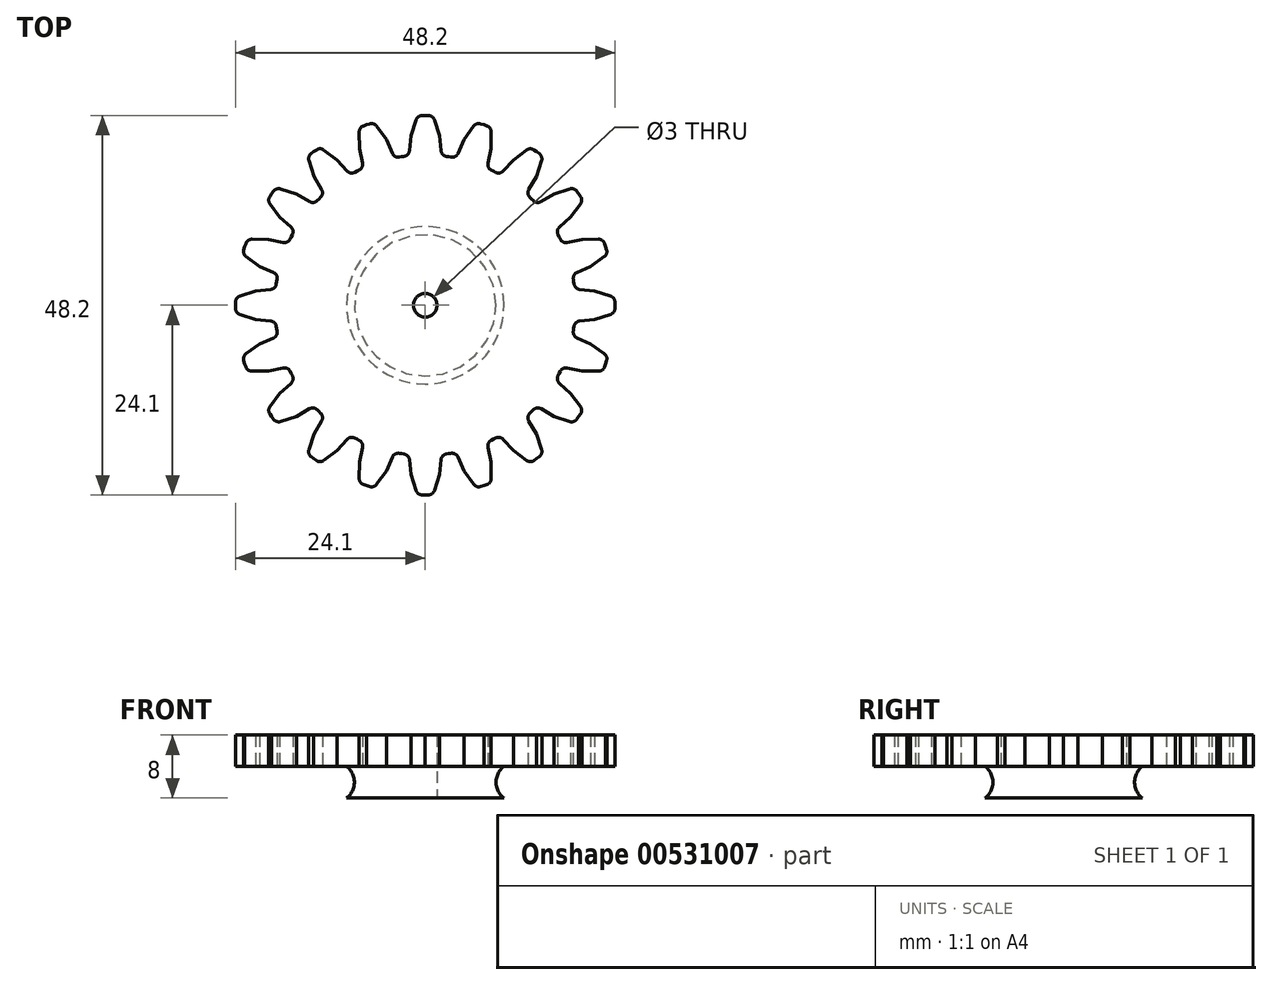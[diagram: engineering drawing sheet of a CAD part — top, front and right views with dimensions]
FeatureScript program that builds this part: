
annotation { "Feature Type Name" : "Feature", "Feature Type Description" : "" }
export const myFeature = defineFeature(function(context is Context, id is Id, definition is map)
    precondition{}
    {
        {
            assignVariable(context, id + "F0", {"name" : "nzuba", "anyValue" : 20});
        }
        {
            var Q0;
            Q0=qCreatedBy(makeId("Front.planeOp"),FACE);
            var sketch = newSketch(context, id + "F1", { "sketchPlane" : qUnion([Q0])});
            skLineSegment(sketch, "E0", {"start": v(0, 0) * mm, "end": v(0, 4) * mm, "construction": true});
            skSolve(sketch);
        }
        {
            var Q0;
            Q0=qCreatedBy(makeId("Top.planeOp"),FACE);
            var sketch = newSketch(context, id + "F2", { "sketchPlane" : qUnion([Q0])});
            skArc(sketch, "E1", {"start": v(18.86, 3) * mm, "mid": v(-19.1, 0) * mm, "end": v(18.86, -3) * mm});
            skCircle(sketch, "E2", {"center": v(0, 0) * mm, "radius": 24.1 * mm, "construction": true});
            skCircle(sketch, "E3", {"center": v(0, 0) * mm, "radius": 21.6 * mm, "construction": true});
            skLineSegment(sketch, "E4", {"start": v(0, 19.1) * mm, "end": v(0, 24.1) * mm, "construction": true});
            skLineSegment(sketch, "E5", {"start": v(-3.68, 23.82) * mm, "end": v(-3.3, 21.35) * mm, "construction": true});
            skLineSegment(sketch, "E6", {"start": v(-3.3, 21.35) * mm, "end": v(-2.92, 18.87) * mm, "construction": true});
            skLineSegment(sketch, "E7", {"start": v(0, 0) * mm, "end": v(24.1, 0) * mm, "construction": true});
            skLineSegment(sketch, "E8", {"start": v(0, 0) * mm, "end": v(18.86, 3) * mm});
            skLineSegment(sketch, "E9", {"start": v(0, 0) * mm, "end": v(19.62, 2) * mm, "construction": true});
            skPoint(sketch, "E10", {"position": v(19, 1.94) * mm});
            skLineSegment(sketch, "E11", {"start": v(19.62, 2) * mm, "end": v(21.52, 1.8) * mm});
            skLineSegment(sketch, "E12", {"start": v(21.52, 1.8) * mm, "end": v(23.53, 1.17) * mm});
            skLineSegment(sketch, "E13", {"start": v(24.09, 0.43) * mm, "end": v(24.1, 0) * mm});
            skPoint(sketch, "E14.visualSharp", {"position": v(24.08, 1) * mm});
            skArc(sketch, "E14.filletArc", {"start": v(24.09, 0.43) * mm, "mid": v(23.93, 0.89) * mm, "end": v(23.53, 1.17) * mm});
            skLineSegment(sketch, "E15.MirrorCS", {"start": v(19.62, -2) * mm, "end": v(21.52, -1.8) * mm});
            skLineSegment(sketch, "E16.MirrorCS", {"start": v(21.52, -1.8) * mm, "end": v(23.53, -1.17) * mm});
            skArc(sketch, "E17.MirrorCS", {"start": v(24.09, -0.43) * mm, "mid": v(23.93, -0.89) * mm, "end": v(23.53, -1.17) * mm});
            skLineSegment(sketch, "E18.MirrorCS", {"start": v(24.09, -0.43) * mm, "end": v(24.1, 0) * mm});
            skLineSegment(sketch, "E19.MirrorCS", {"start": v(0, 0) * mm, "end": v(18.86, -3) * mm});
            skCircle(sketch, "E20", {"center": v(0, 0) * mm, "radius": 1.5 * mm});
            skLineSegment(sketch, "E21", {"start": v(18.86, 3) * mm, "end": v(18.91, 2.67) * mm});
            skArc(sketch, "E22", {"start": v(18.91, 2.67) * mm, "mid": v(19.15, 2.22) * mm, "end": v(19.62, 2) * mm});
            skLineSegment(sketch, "E23.MirrorCS", {"start": v(18.86, -3) * mm, "end": v(18.91, -2.67) * mm});
            skArc(sketch, "E24.MirrorCS", {"start": v(18.91, -2.67) * mm, "mid": v(19.15, -2.22) * mm, "end": v(19.62, -2) * mm});
            skSolve(sketch);
        }
        {
            var Q0;
            Q0=makeQuery(id+"F2.imprint","IMPRINT",FACE,{"disambiguationData":[TD([[makeQuery(id+"F2.imprint","IMPRINT",EDGE,{"derivedFrom":sQuery(id+"F2.wireOp",EDGE,"E11")}),-1.0]])]});
            extrude(context, id + "F3", {"entities" : qUnion([Q0]), "depth" : 4 * mm, "offsetDistance" : 25 * mm});
        }
        {
            var Q0;
            Q0=makeQuery(id+"F3.opExtrude","SWEPT_BODY",BODY,{"disambiguationData":[OSD([sQuery(id+"F2.wireOp",EDGE,"E8"),sQuery(id+"F2.wireOp",EDGE,"Ccr5RPwP-yEiI-mMhH-aCbI-xiKkbVCYuAfT"),sQuery(id+"F2.wireOp",EDGE,"E11"),sQuery(id+"F2.wireOp",EDGE,"E12"),sQuery(id+"F2.wireOp",EDGE,"E13"),sQuery(id+"F2.wireOp",EDGE,"E14.filletArc"),sQuery(id+"F2.wireOp",EDGE,"434113d8-d490-4e0a-a8ba-07c452dbb1c90.MirrorCS"),sQuery(id+"F2.wireOp",EDGE,"E15.MirrorCS"),sQuery(id+"F2.wireOp",EDGE,"E16.MirrorCS"),sQuery(id+"F2.wireOp",EDGE,"E17.MirrorCS"),sQuery(id+"F2.wireOp",EDGE,"E18.MirrorCS"),sQuery(id+"F2.wireOp",EDGE,"E19.MirrorCS")])]});
            var Q1;
            Q1=sQuery(id+"F1.wireOp",EDGE,"E0");
            circularPattern(context, id + "F4", {"operationType" : NewBodyOperationType.ADD, "entities" : qUnion([Q0]), "axis" : qUnion([Q1]), "angle" : 360 * degree, "instanceCount" : getVariable(context, 'nzuba'), "equalSpace" : true, "computeTransformsWithoutBuiltin" : true});
        }
        {
            var Q0;
            Q0=qCreatedBy(makeId("Front.planeOp"),FACE);
            var sketch = newSketch(context, id + "F5", { "sketchPlane" : qUnion([Q0])});
            skLineSegment(sketch, "E25", {"start": v(0, 0) * mm, "end": v(0, -4) * mm});
            skLineSegment(sketch, "E26", {"start": v(0, -4) * mm, "end": v(10, -4) * mm});
            skLineSegment(sketch, "E27", {"start": v(0, 0) * mm, "end": v(10, 0) * mm});
            skArc(sketch, "E28", {"start": v(10, 0) * mm, "mid": v(9, -2) * mm, "end": v(10, -4) * mm});
            skSolve(sketch);
        }
        {
            var Q0;
            Q0=makeQuery(id+"F5.imprint","IMPRINT",FACE,{"disambiguationData":[TD([[makeQuery(id+"F5.imprint","IMPRINT",EDGE,{"derivedFrom":sQuery(id+"F5.wireOp",EDGE,"E25")}),1.0]])]});
            var Q1;
            Q1=sQuery(id+"F5.wireOp",EDGE,"E25");
            revolve(context, id + "F6", {"operationType" : NewBodyOperationType.ADD, "surfaceOperationType" : NewSurfaceOperationType.NEW, "entities" : qUnion([Q0]), "axis" : qUnion([Q1]), "revolveType" : RevolveType.FULL});
        }
        {
            var Q0;
            Q0=makeQuery(id+"F6.opRevolve","SWEPT_FACE",FACE,{"disambiguationData":[OSD([sQuery(id+"F5.wireOp",EDGE,"E27")])]});
            var Q1;
            Q1=makeQuery(id+"F6.opRevolve","SWEPT_FACE",FACE,{"disambiguationData":[OSD([sQuery(id+"F5.wireOp",EDGE,"E26")])]});
            extrude(context, id + "F7", {"entities" : qUnion([Q0]), "operationType" : NewBodyOperationType.REMOVE, "endBound" : BoundingType.UP_TO_SURFACE, "oppositeDirection" : true, "depth" : 25 * mm, "endBoundEntityFace" : qUnion([Q1]), "offsetDistance" : 25 * mm});
        }
    });
